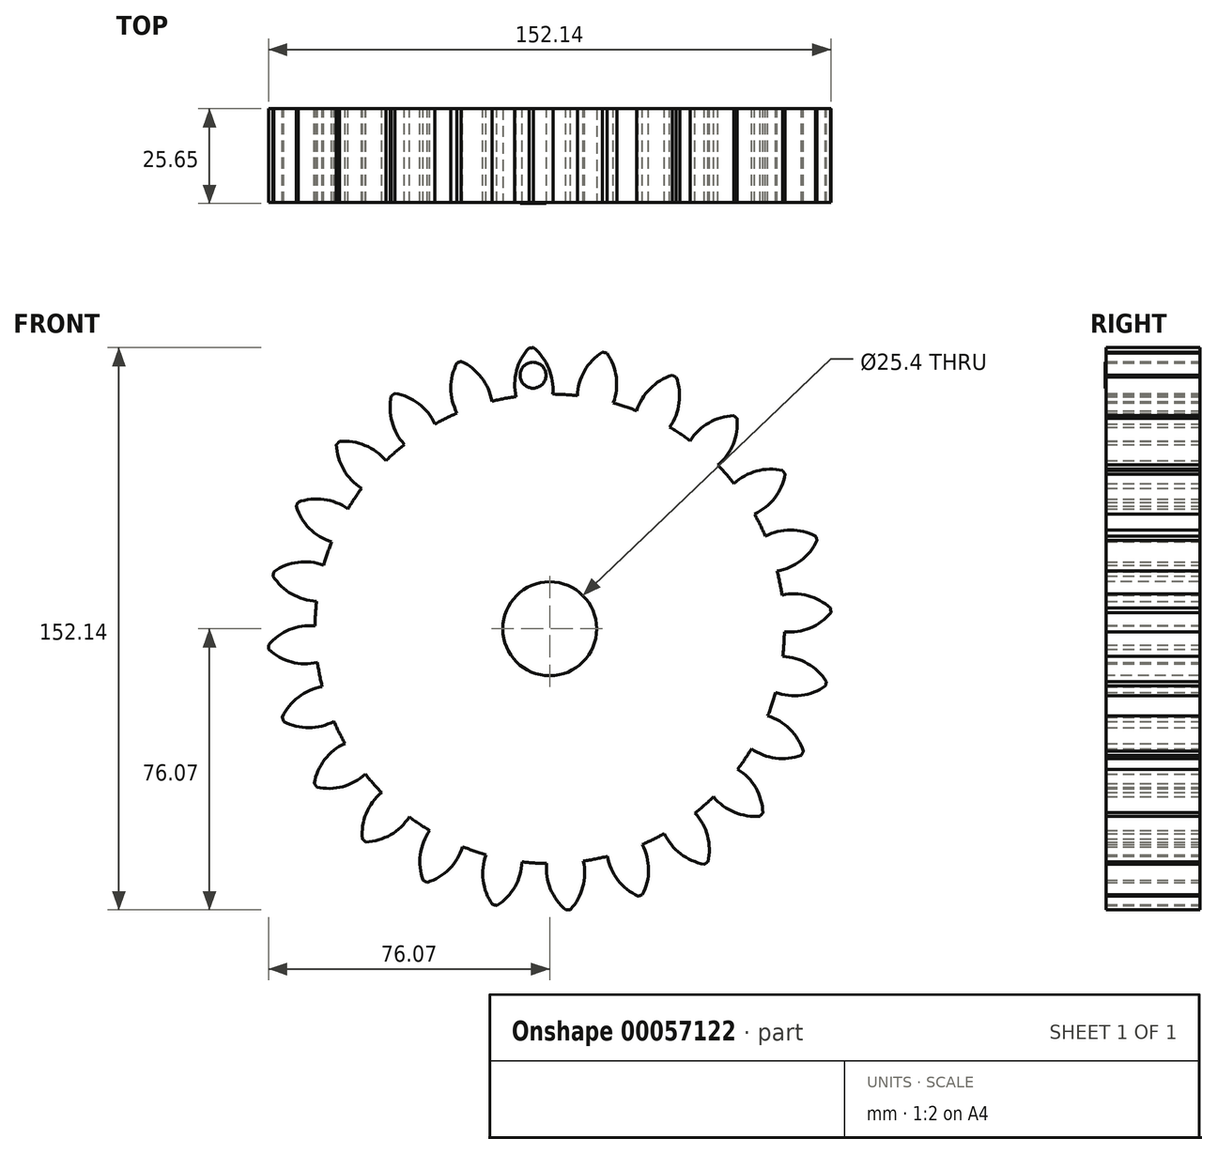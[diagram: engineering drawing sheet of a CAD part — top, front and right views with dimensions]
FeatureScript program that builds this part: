
annotation { "Feature Type Name" : "Feature", "Feature Type Description" : "" }
export const myFeature = defineFeature(function(context is Context, id is Id, definition is map)
    precondition{}
    {
        {
            var Q0;
            Q0=qCreatedBy(makeId("Front.planeOp"),FACE);
            var sketch = newSketch(context, id + "F0", { "sketchPlane" : qUnion([Q0])});
            skPoint(sketch, "E0.rect.middle", {"position": v(0, 0) * mm});
            skLineSegment(sketch, "E1", {"start": v(0, 0) * mm, "end": v(0, 76.2) * mm});
            skLineSegment(sketch, "E2", {"start": v(0, 0) * mm, "end": v(0, -76.2) * mm});
            skLineSegment(sketch, "E3", {"start": v(0, 0) * mm, "end": v(19.72, 73.6) * mm});
            skLineSegment(sketch, "E4", {"start": v(0, 0) * mm, "end": v(38.1, 66) * mm});
            skLineSegment(sketch, "E5", {"start": v(0, 0) * mm, "end": v(53.88, 53.88) * mm});
            skLineSegment(sketch, "E6", {"start": v(0, 0) * mm, "end": v(66, 38.1) * mm});
            skLineSegment(sketch, "E7", {"start": v(0, 0) * mm, "end": v(73.6, 19.72) * mm});
            skLineSegment(sketch, "E8", {"start": v(0, 0) * mm, "end": v(76.2, 0) * mm});
            skLineSegment(sketch, "E9", {"start": v(0, 0) * mm, "end": v(73.6, -19.72) * mm});
            skLineSegment(sketch, "E10", {"start": v(0, 0) * mm, "end": v(66, -38.1) * mm});
            skLineSegment(sketch, "E11", {"start": v(0, 0) * mm, "end": v(53.88, -53.88) * mm});
            skLineSegment(sketch, "E12", {"start": v(0, 0) * mm, "end": v(38.1, -66) * mm});
            skLineSegment(sketch, "E13", {"start": v(0, 0) * mm, "end": v(19.72, -73.6) * mm});
            skLineSegment(sketch, "E14", {"start": v(0, 0) * mm, "end": v(-19.72, -73.6) * mm});
            skLineSegment(sketch, "E15", {"start": v(0, 0) * mm, "end": v(-38.1, -66) * mm});
            skLineSegment(sketch, "E16", {"start": v(0, 0) * mm, "end": v(-53.88, -53.88) * mm});
            skLineSegment(sketch, "E17", {"start": v(0, 0) * mm, "end": v(-66, -38.1) * mm});
            skLineSegment(sketch, "E18", {"start": v(0, 0) * mm, "end": v(-73.6, -19.72) * mm});
            skLineSegment(sketch, "E19", {"start": v(0, 0) * mm, "end": v(-76.2, 0.07) * mm});
            skLineSegment(sketch, "E20", {"start": v(0, 0) * mm, "end": v(-73.6, 19.72) * mm});
            skLineSegment(sketch, "E21", {"start": v(0, 0) * mm, "end": v(-66, 38.1) * mm});
            skLineSegment(sketch, "E22", {"start": v(0, 0) * mm, "end": v(-53.88, 53.88) * mm});
            skLineSegment(sketch, "E23", {"start": v(0, 0) * mm, "end": v(-38.1, 66) * mm});
            skLineSegment(sketch, "E24", {"start": v(0, 0) * mm, "end": v(-19.72, 73.6) * mm});
            skCircle(sketch, "E25", {"center": v(0, 0) * mm, "radius": 76.2 * mm});
            skCircle(sketch, "E26", {"center": v(0, 0) * mm, "radius": 69.85 * mm});
            skCircle(sketch, "E27", {"center": v(0, 0) * mm, "radius": 63.5 * mm});
            skLineSegment(sketch, "E28", {"start": v(0, 0) * mm, "end": v(-4.98, 76.04) * mm});
            skLineSegment(sketch, "E29", {"start": v(0, 69.85) * mm, "end": v(-76.58, 69.85) * mm});
            skLineSegment(sketch, "E30", {"start": v(0, 69.85) * mm, "end": v(-76.5, 42) * mm});
            skLineSegment(sketch, "E31", {"start": v(-4.98, 76.04) * mm, "end": v(-7.15, 109.16) * mm});
            skLineSegment(sketch, "E32", {"start": v(0, 76.2) * mm, "end": v(0, 110.22) * mm});
            skCircle(sketch, "E33", {"center": v(0, 69.85) * mm, "radius": 14.6 * mm});
            skPoint(sketch, "E34", {"position": v(-13.72, 64.85) * mm});
            skArc(sketch, "E35", {"start": v(0.82, 63.5) * mm, "mid": v(-0.22, 70.43) * mm, "end": v(-4.37, 76.07) * mm});
            skArc(sketch, "E36.MirrorCS", {"start": v(-9.1, 62.84) * mm, "mid": v(-8.97, 69.85) * mm, "end": v(-5.6, 76) * mm});
            skSolve(sketch);
        }
        {
            var Q0;
            {var subQ1=sQuery(id+"F0.wireOp",EDGE,"E23");var subQ3=sQuery(id+"F0.wireOp",EDGE,"E27");var subQ4=makeQuery(id+"F0.imprint","INTERSECT",VERTEX,{"derivedFrom":[subQ1,subQ3]});Q0=makeQuery(id+"F0.imprint","IMPRINT",FACE,{"disambiguationData":[TD([[makeQuery(id+"F0.imprint","IMPRINT",EDGE,{"disambiguationData":[TD([[subQ4,1.0]])],"derivedFrom":subQ3}),1.0]])]});}
            var Q1;
            {var subQ1=sQuery(id+"F0.wireOp",EDGE,"E22");var subQ3=sQuery(id+"F0.wireOp",EDGE,"E27");var subQ4=makeQuery(id+"F0.imprint","INTERSECT",VERTEX,{"derivedFrom":[subQ1,subQ3]});Q1=makeQuery(id+"F0.imprint","IMPRINT",FACE,{"disambiguationData":[TD([[makeQuery(id+"F0.imprint","IMPRINT",EDGE,{"disambiguationData":[TD([[subQ4,1.0]])],"derivedFrom":subQ3}),1.0]])]});}
            var Q2;
            {var subQ1=sQuery(id+"F0.wireOp",EDGE,"E1");var subQ3=sQuery(id+"F0.wireOp",EDGE,"E33");var subQ4=makeQuery(id+"F0.imprint","INTERSECT",VERTEX,{"derivedFrom":[subQ1,subQ3]});Q2=makeQuery(id+"F0.imprint","IMPRINT",FACE,{"disambiguationData":[TD([[makeQuery(id+"F0.imprint","IMPRINT",EDGE,{"disambiguationData":[TD([[subQ4,1.0]])],"derivedFrom":subQ3}),-1.0]])]});}
            var Q3;
            {var subQ1=sQuery(id+"F0.wireOp",EDGE,"E19");var subQ3=sQuery(id+"F0.wireOp",EDGE,"E27");var subQ4=makeQuery(id+"F0.imprint","INTERSECT",VERTEX,{"derivedFrom":[subQ1,subQ3]});Q3=makeQuery(id+"F0.imprint","IMPRINT",FACE,{"disambiguationData":[TD([[makeQuery(id+"F0.imprint","IMPRINT",EDGE,{"disambiguationData":[TD([[subQ4,1.0]])],"derivedFrom":subQ3}),1.0]])]});}
            var Q4;
            {var subQ1=sQuery(id+"F0.wireOp",EDGE,"E24");var subQ3=sQuery(id+"F0.wireOp",EDGE,"E27");var subQ4=makeQuery(id+"F0.imprint","INTERSECT",VERTEX,{"derivedFrom":[subQ1,subQ3]});Q4=makeQuery(id+"F0.imprint","IMPRINT",FACE,{"disambiguationData":[TD([[makeQuery(id+"F0.imprint","IMPRINT",EDGE,{"disambiguationData":[TD([[subQ4,1.0]])],"derivedFrom":subQ3}),1.0]])]});}
            var Q5;
            {var subQ1=sQuery(id+"F0.wireOp",EDGE,"E20");var subQ3=sQuery(id+"F0.wireOp",EDGE,"E27");var subQ4=makeQuery(id+"F0.imprint","INTERSECT",VERTEX,{"derivedFrom":[subQ1,subQ3]});Q5=makeQuery(id+"F0.imprint","IMPRINT",FACE,{"disambiguationData":[TD([[makeQuery(id+"F0.imprint","IMPRINT",EDGE,{"disambiguationData":[TD([[subQ4,1.0]])],"derivedFrom":subQ3}),1.0]])]});}
            var Q6;
            {var subQ1=sQuery(id+"F0.wireOp",EDGE,"E21");var subQ3=sQuery(id+"F0.wireOp",EDGE,"E27");var subQ4=makeQuery(id+"F0.imprint","INTERSECT",VERTEX,{"derivedFrom":[subQ1,subQ3]});Q6=makeQuery(id+"F0.imprint","IMPRINT",FACE,{"disambiguationData":[TD([[makeQuery(id+"F0.imprint","IMPRINT",EDGE,{"disambiguationData":[TD([[subQ4,1.0]])],"derivedFrom":subQ3}),1.0]])]});}
            var Q7;
            {var subQ1=sQuery(id+"F0.wireOp",EDGE,"E6");var subQ3=sQuery(id+"F0.wireOp",EDGE,"E27");var subQ4=makeQuery(id+"F0.imprint","INTERSECT",VERTEX,{"derivedFrom":[subQ1,subQ3]});Q7=makeQuery(id+"F0.imprint","IMPRINT",FACE,{"disambiguationData":[TD([[makeQuery(id+"F0.imprint","IMPRINT",EDGE,{"disambiguationData":[TD([[subQ4,1.0]])],"derivedFrom":subQ3}),1.0]])]});}
            var Q8;
            {var subQ1=sQuery(id+"F0.wireOp",EDGE,"E4");var subQ3=sQuery(id+"F0.wireOp",EDGE,"E27");var subQ4=makeQuery(id+"F0.imprint","INTERSECT",VERTEX,{"derivedFrom":[subQ1,subQ3]});Q8=makeQuery(id+"F0.imprint","IMPRINT",FACE,{"disambiguationData":[TD([[makeQuery(id+"F0.imprint","IMPRINT",EDGE,{"disambiguationData":[TD([[subQ4,1.0]])],"derivedFrom":subQ3}),1.0]])]});}
            var Q9;
            {var subQ1=sQuery(id+"F0.wireOp",EDGE,"E7");var subQ3=sQuery(id+"F0.wireOp",EDGE,"E27");var subQ4=makeQuery(id+"F0.imprint","INTERSECT",VERTEX,{"derivedFrom":[subQ1,subQ3]});Q9=makeQuery(id+"F0.imprint","IMPRINT",FACE,{"disambiguationData":[TD([[makeQuery(id+"F0.imprint","IMPRINT",EDGE,{"disambiguationData":[TD([[subQ4,1.0]])],"derivedFrom":subQ3}),1.0]])]});}
            var Q10;
            {var subQ0=sQuery(id+"F0.wireOp",EDGE,"E3");var subQ5=sQuery(id+"F0.wireOp",EDGE,"E27");var subQ6=makeQuery(id+"F0.imprint","INTERSECT",VERTEX,{"derivedFrom":[subQ0,subQ5]});Q10=makeQuery(id+"F0.imprint","IMPRINT",FACE,{"disambiguationData":[TD([[makeQuery(id+"F0.imprint","IMPRINT",EDGE,{"disambiguationData":[TD([[subQ6,-1.0]])],"derivedFrom":subQ5}),1.0]])]});}
            var Q11;
            {var subQ1=sQuery(id+"F0.wireOp",EDGE,"E3");var subQ3=sQuery(id+"F0.wireOp",EDGE,"E27");var subQ4=makeQuery(id+"F0.imprint","INTERSECT",VERTEX,{"derivedFrom":[subQ1,subQ3]});Q11=makeQuery(id+"F0.imprint","IMPRINT",FACE,{"disambiguationData":[TD([[makeQuery(id+"F0.imprint","IMPRINT",EDGE,{"disambiguationData":[TD([[subQ4,1.0]])],"derivedFrom":subQ3}),1.0]])]});}
            var Q12;
            {var subQ1=sQuery(id+"F0.wireOp",EDGE,"E5");var subQ3=sQuery(id+"F0.wireOp",EDGE,"E27");var subQ4=makeQuery(id+"F0.imprint","INTERSECT",VERTEX,{"derivedFrom":[subQ1,subQ3]});Q12=makeQuery(id+"F0.imprint","IMPRINT",FACE,{"disambiguationData":[TD([[makeQuery(id+"F0.imprint","IMPRINT",EDGE,{"disambiguationData":[TD([[subQ4,1.0]])],"derivedFrom":subQ3}),1.0]])]});}
            var Q13;
            {var subQ1=sQuery(id+"F0.wireOp",EDGE,"E17");var subQ3=sQuery(id+"F0.wireOp",EDGE,"E27");var subQ4=makeQuery(id+"F0.imprint","INTERSECT",VERTEX,{"derivedFrom":[subQ1,subQ3]});Q13=makeQuery(id+"F0.imprint","IMPRINT",FACE,{"disambiguationData":[TD([[makeQuery(id+"F0.imprint","IMPRINT",EDGE,{"disambiguationData":[TD([[subQ4,1.0]])],"derivedFrom":subQ3}),1.0]])]});}
            var Q14;
            {var subQ1=sQuery(id+"F0.wireOp",EDGE,"E15");var subQ3=sQuery(id+"F0.wireOp",EDGE,"E27");var subQ4=makeQuery(id+"F0.imprint","INTERSECT",VERTEX,{"derivedFrom":[subQ1,subQ3]});Q14=makeQuery(id+"F0.imprint","IMPRINT",FACE,{"disambiguationData":[TD([[makeQuery(id+"F0.imprint","IMPRINT",EDGE,{"disambiguationData":[TD([[subQ4,1.0]])],"derivedFrom":subQ3}),1.0]])]});}
            var Q15;
            {var subQ1=sQuery(id+"F0.wireOp",EDGE,"E16");var subQ3=sQuery(id+"F0.wireOp",EDGE,"E27");var subQ4=makeQuery(id+"F0.imprint","INTERSECT",VERTEX,{"derivedFrom":[subQ1,subQ3]});Q15=makeQuery(id+"F0.imprint","IMPRINT",FACE,{"disambiguationData":[TD([[makeQuery(id+"F0.imprint","IMPRINT",EDGE,{"disambiguationData":[TD([[subQ4,1.0]])],"derivedFrom":subQ3}),1.0]])]});}
            var Q16;
            {var subQ1=sQuery(id+"F0.wireOp",EDGE,"E2");var subQ3=sQuery(id+"F0.wireOp",EDGE,"E27");var subQ4=makeQuery(id+"F0.imprint","INTERSECT",VERTEX,{"derivedFrom":[subQ1,subQ3]});Q16=makeQuery(id+"F0.imprint","IMPRINT",FACE,{"disambiguationData":[TD([[makeQuery(id+"F0.imprint","IMPRINT",EDGE,{"disambiguationData":[TD([[subQ4,1.0]])],"derivedFrom":subQ3}),1.0]])]});}
            var Q17;
            {var subQ1=sQuery(id+"F0.wireOp",EDGE,"E14");var subQ3=sQuery(id+"F0.wireOp",EDGE,"E27");var subQ4=makeQuery(id+"F0.imprint","INTERSECT",VERTEX,{"derivedFrom":[subQ1,subQ3]});Q17=makeQuery(id+"F0.imprint","IMPRINT",FACE,{"disambiguationData":[TD([[makeQuery(id+"F0.imprint","IMPRINT",EDGE,{"disambiguationData":[TD([[subQ4,1.0]])],"derivedFrom":subQ3}),1.0]])]});}
            var Q18;
            {var subQ1=sQuery(id+"F0.wireOp",EDGE,"E18");var subQ3=sQuery(id+"F0.wireOp",EDGE,"E27");var subQ4=makeQuery(id+"F0.imprint","INTERSECT",VERTEX,{"derivedFrom":[subQ1,subQ3]});Q18=makeQuery(id+"F0.imprint","IMPRINT",FACE,{"disambiguationData":[TD([[makeQuery(id+"F0.imprint","IMPRINT",EDGE,{"disambiguationData":[TD([[subQ4,1.0]])],"derivedFrom":subQ3}),1.0]])]});}
            var Q19;
            {var subQ0=sQuery(id+"F0.wireOp",EDGE,"E33");var subQ1=sQuery(id+"F0.wireOp",EDGE,"E1");var subQ2=makeQuery(id+"F0.imprint","INTERSECT",VERTEX,{"derivedFrom":[subQ1,subQ0]});Q19=makeQuery(id+"F0.imprint","IMPRINT",FACE,{"disambiguationData":[TD([[makeQuery(id+"F0.imprint","IMPRINT",EDGE,{"disambiguationData":[TD([[subQ2,-1.0]])],"derivedFrom":subQ1}),1.0]])]});}
            var Q20;
            {var subQ0=sQuery(id+"F0.wireOp",EDGE,"E27");var subQ1=makeQuery(id+"F0.imprint","INTERSECT",VERTEX,{"derivedFrom":[subQ0,sQuery(id+"F0.wireOp",EDGE,"E36.MirrorCS")]});Q20=makeQuery(id+"F0.imprint","IMPRINT",FACE,{"disambiguationData":[TD([[makeQuery(id+"F0.imprint","IMPRINT",EDGE,{"disambiguationData":[TD([[subQ1,1.0]])],"derivedFrom":subQ0}),1.0]])]});}
            var Q21;
            {var subQ0=sQuery(id+"F0.wireOp",EDGE,"E33");var subQ1=sQuery(id+"F0.wireOp",EDGE,"E1");var subQ2=makeQuery(id+"F0.imprint","INTERSECT",VERTEX,{"derivedFrom":[subQ1,subQ0]});Q21=makeQuery(id+"F0.imprint","IMPRINT",FACE,{"disambiguationData":[TD([[makeQuery(id+"F0.imprint","IMPRINT",EDGE,{"disambiguationData":[TD([[subQ2,-1.0]])],"derivedFrom":subQ1}),-1.0]])]});}
            var Q22;
            {var subQ1=sQuery(id+"F0.wireOp",EDGE,"E1");var subQ3=sQuery(id+"F0.wireOp",EDGE,"E27");var subQ4=makeQuery(id+"F0.imprint","INTERSECT",VERTEX,{"derivedFrom":[subQ1,subQ3]});Q22=makeQuery(id+"F0.imprint","IMPRINT",FACE,{"disambiguationData":[TD([[makeQuery(id+"F0.imprint","IMPRINT",EDGE,{"disambiguationData":[TD([[subQ4,-1.0]])],"derivedFrom":subQ3}),-1.0]])]});}
            var Q23;
            {var subQ0=sQuery(id+"F0.wireOp",EDGE,"E36.MirrorCS");var subQ1=sQuery(id+"F0.wireOp",EDGE,"E27");var subQ2=makeQuery(id+"F0.imprint","INTERSECT",VERTEX,{"derivedFrom":[subQ1,subQ0]});Q23=makeQuery(id+"F0.imprint","IMPRINT",FACE,{"disambiguationData":[TD([[makeQuery(id+"F0.imprint","IMPRINT",EDGE,{"disambiguationData":[TD([[subQ2,1.0]])],"derivedFrom":subQ1}),-1.0]])]});}
            var Q24;
            {var subQ0=sQuery(id+"F0.wireOp",EDGE,"E28");var subQ1=sQuery(id+"F0.wireOp",EDGE,"E26");var subQ2=makeQuery(id+"F0.imprint","INTERSECT",VERTEX,{"derivedFrom":[subQ1,subQ0]});Q24=makeQuery(id+"F0.imprint","IMPRINT",FACE,{"disambiguationData":[TD([[makeQuery(id+"F0.imprint","IMPRINT",EDGE,{"disambiguationData":[TD([[subQ2,-1.0]])],"derivedFrom":subQ1}),1.0]])]});}
            var Q25;
            {var subQ0=sQuery(id+"F0.wireOp",EDGE,"E28");var subQ1=sQuery(id+"F0.wireOp",EDGE,"E26");var subQ2=makeQuery(id+"F0.imprint","INTERSECT",VERTEX,{"derivedFrom":[subQ1,subQ0]});Q25=makeQuery(id+"F0.imprint","IMPRINT",FACE,{"disambiguationData":[TD([[makeQuery(id+"F0.imprint","IMPRINT",EDGE,{"disambiguationData":[TD([[subQ2,-1.0]])],"derivedFrom":subQ1}),-1.0]])]});}
            var Q26;
            {var subQ0=sQuery(id+"F0.wireOp",EDGE,"E28");var subQ5=sQuery(id+"F0.wireOp",EDGE,"E29");var subQ6=makeQuery(id+"F0.imprint","INTERSECT",VERTEX,{"derivedFrom":[subQ0,subQ5]});Q26=makeQuery(id+"F0.imprint","IMPRINT",FACE,{"disambiguationData":[TD([[makeQuery(id+"F0.imprint","IMPRINT",EDGE,{"disambiguationData":[TD([[subQ6,-1.0]])],"derivedFrom":subQ5}),-1.0]])]});}
            var Q27;
            {var subQ1=sQuery(id+"F0.wireOp",EDGE,"E25");var subQ3=sQuery(id+"F0.wireOp",EDGE,"E35");var subQ4=makeQuery(id+"F0.imprint","INTERSECT",VERTEX,{"derivedFrom":[subQ1,subQ3]});Q27=makeQuery(id+"F0.imprint","IMPRINT",FACE,{"disambiguationData":[TD([[makeQuery(id+"F0.imprint","IMPRINT",EDGE,{"disambiguationData":[TD([[subQ4,-1.0]])],"derivedFrom":subQ1}),1.0]])]});}
            var Q28;
            {var subQ0=sQuery(id+"F0.wireOp",EDGE,"E35");var subQ3=sQuery(id+"F0.wireOp",EDGE,"E27");var subQ5=makeQuery(id+"F0.imprint","INTERSECT",VERTEX,{"derivedFrom":[subQ3,subQ0]});Q28=makeQuery(id+"F0.imprint","IMPRINT",FACE,{"disambiguationData":[TD([[makeQuery(id+"F0.imprint","IMPRINT",EDGE,{"disambiguationData":[TD([[subQ5,-1.0]])],"derivedFrom":subQ3}),-1.0]])]});}
            var Q29;
            {var subQ1=sQuery(id+"F0.wireOp",EDGE,"E26");var subQ3=sQuery(id+"F0.wireOp",EDGE,"E28");var subQ4=makeQuery(id+"F0.imprint","INTERSECT",VERTEX,{"derivedFrom":[subQ1,subQ3]});Q29=makeQuery(id+"F0.imprint","IMPRINT",FACE,{"disambiguationData":[TD([[makeQuery(id+"F0.imprint","IMPRINT",EDGE,{"disambiguationData":[TD([[subQ4,-1.0]])],"derivedFrom":subQ3}),-1.0]])]});}
            var Q30;
            {var subQ1=sQuery(id+"F0.wireOp",EDGE,"E26");var subQ3=sQuery(id+"F0.wireOp",EDGE,"E28");var subQ4=makeQuery(id+"F0.imprint","INTERSECT",VERTEX,{"derivedFrom":[subQ1,subQ3]});Q30=makeQuery(id+"F0.imprint","IMPRINT",FACE,{"disambiguationData":[TD([[makeQuery(id+"F0.imprint","IMPRINT",EDGE,{"disambiguationData":[TD([[subQ4,1.0]])],"derivedFrom":subQ3}),-1.0]])]});}
            var Q31;
            {var subQ1=sQuery(id+"F0.wireOp",EDGE,"E10");var subQ3=sQuery(id+"F0.wireOp",EDGE,"E27");var subQ4=makeQuery(id+"F0.imprint","INTERSECT",VERTEX,{"derivedFrom":[subQ1,subQ3]});Q31=makeQuery(id+"F0.imprint","IMPRINT",FACE,{"disambiguationData":[TD([[makeQuery(id+"F0.imprint","IMPRINT",EDGE,{"disambiguationData":[TD([[subQ4,1.0]])],"derivedFrom":subQ3}),1.0]])]});}
            var Q32;
            {var subQ1=sQuery(id+"F0.wireOp",EDGE,"E9");var subQ3=sQuery(id+"F0.wireOp",EDGE,"E27");var subQ4=makeQuery(id+"F0.imprint","INTERSECT",VERTEX,{"derivedFrom":[subQ1,subQ3]});Q32=makeQuery(id+"F0.imprint","IMPRINT",FACE,{"disambiguationData":[TD([[makeQuery(id+"F0.imprint","IMPRINT",EDGE,{"disambiguationData":[TD([[subQ4,1.0]])],"derivedFrom":subQ3}),1.0]])]});}
            var Q33;
            {var subQ1=sQuery(id+"F0.wireOp",EDGE,"E8");var subQ3=sQuery(id+"F0.wireOp",EDGE,"E27");var subQ4=makeQuery(id+"F0.imprint","INTERSECT",VERTEX,{"derivedFrom":[subQ1,subQ3]});Q33=makeQuery(id+"F0.imprint","IMPRINT",FACE,{"disambiguationData":[TD([[makeQuery(id+"F0.imprint","IMPRINT",EDGE,{"disambiguationData":[TD([[subQ4,1.0]])],"derivedFrom":subQ3}),1.0]])]});}
            var Q34;
            {var subQ1=sQuery(id+"F0.wireOp",EDGE,"E11");var subQ3=sQuery(id+"F0.wireOp",EDGE,"E27");var subQ4=makeQuery(id+"F0.imprint","INTERSECT",VERTEX,{"derivedFrom":[subQ1,subQ3]});Q34=makeQuery(id+"F0.imprint","IMPRINT",FACE,{"disambiguationData":[TD([[makeQuery(id+"F0.imprint","IMPRINT",EDGE,{"disambiguationData":[TD([[subQ4,1.0]])],"derivedFrom":subQ3}),1.0]])]});}
            var Q35;
            {var subQ1=sQuery(id+"F0.wireOp",EDGE,"E2");var subQ3=sQuery(id+"F0.wireOp",EDGE,"E27");var subQ4=makeQuery(id+"F0.imprint","INTERSECT",VERTEX,{"derivedFrom":[subQ1,subQ3]});Q35=makeQuery(id+"F0.imprint","IMPRINT",FACE,{"disambiguationData":[TD([[makeQuery(id+"F0.imprint","IMPRINT",EDGE,{"disambiguationData":[TD([[subQ4,-1.0]])],"derivedFrom":subQ3}),1.0]])]});}
            var Q36;
            {var subQ1=sQuery(id+"F0.wireOp",EDGE,"E12");var subQ3=sQuery(id+"F0.wireOp",EDGE,"E27");var subQ4=makeQuery(id+"F0.imprint","INTERSECT",VERTEX,{"derivedFrom":[subQ1,subQ3]});Q36=makeQuery(id+"F0.imprint","IMPRINT",FACE,{"disambiguationData":[TD([[makeQuery(id+"F0.imprint","IMPRINT",EDGE,{"disambiguationData":[TD([[subQ4,1.0]])],"derivedFrom":subQ3}),1.0]])]});}
            extrude(context, id + "F1", {"entities" : qUnion([Q0, Q1, Q2, Q3, Q4, Q5, Q6, Q7, Q8, Q9, Q10, Q11, Q12, Q13, Q14, Q15, Q16, Q17, Q18, Q19, Q20, Q21, Q22, Q23, Q24, Q25, Q26, Q27, Q28, Q29, Q30, Q31, Q32, Q33, Q34, Q35, Q36]), "depth" : 25.4 * mm, "symmetric" : true});
        }
        {
            var Q0;
            Q0=makeQuery(id+"F1.opExtrude","SWEPT_BODY",BODY,{"disambiguationData":[OSD([sQuery(id+"F0.wireOp",EDGE,"E25"),sQuery(id+"F0.wireOp",EDGE,"E27"),sQuery(id+"F0.wireOp",EDGE,"E35"),sQuery(id+"F0.wireOp",EDGE,"E36.MirrorCS")])]});
            var Q1;
            Q1=makeQuery(id+"F1.opExtrude","SWEPT_FACE",FACE,{"disambiguationData":[OSD([sQuery(id+"F0.wireOp",EDGE,"E27")])]});
            circularPattern(context, id + "F2", {"operationType" : NewBodyOperationType.ADD, "entities" : qUnion([Q0]), "axis" : qUnion([Q1]), "angle" : 15 * degree, "instanceCount" : 24});
        }
        {
            var Q0;
            Q0=makeQuery(id+"F1.opExtrude","CAP_FACE",FACE,{"disambiguationData":[OSD([sQuery(id+"F0.wireOp",EDGE,"E25"),sQuery(id+"F0.wireOp",EDGE,"E27"),sQuery(id+"F0.wireOp",EDGE,"E35"),sQuery(id+"F0.wireOp",EDGE,"E36.MirrorCS")])],"isStart":false});
            var sketch = newSketch(context, id + "F3", { "sketchPlane" : qUnion([Q0])});
            skPoint(sketch, "E37", {"position": v(0, 0) * mm});
            skSolve(sketch);
        }
        {
            var Q0;
            Q0=sQuery(id+"F3.wireOp",VERTEX,"E37");
            var Q1;
            Q1=makeQuery(id+"F1.opExtrude","SWEPT_BODY",BODY,{"disambiguationData":[OSD([sQuery(id+"F0.wireOp",EDGE,"E25"),sQuery(id+"F0.wireOp",EDGE,"E27"),sQuery(id+"F0.wireOp",EDGE,"E35"),sQuery(id+"F0.wireOp",EDGE,"E36.MirrorCS")])]});
            hole(context, id + "F4", {"style" : HoleStyle.SIMPLE, "holeDiameter" : 25.4 * mm, "endStyle" : HoleEndStyle.THROUGH, "locations" : qUnion([Q0]), "scope" : qUnion([Q1])});
        }
        {
            var Q0;
            {var subQ0=makeQuery(id+"F1.opExtrude","CAP_FACE",FACE,{"disambiguationData":[OSD([sQuery(id+"F0.wireOp",EDGE,"E25"),sQuery(id+"F0.wireOp",EDGE,"E27"),sQuery(id+"F0.wireOp",EDGE,"E35"),sQuery(id+"F0.wireOp",EDGE,"E36.MirrorCS")])],"isStart":false});Q0=makeQuery(id+"F2.boolean.opBoolean","MERGE",FACE,{"derivedFrom":[subQ0,makeQuery(id+"F2.opPattern","COPY",FACE,{"derivedFrom":subQ0,"instanceName":"1"}),makeQuery(id+"F2.opPattern","COPY",FACE,{"derivedFrom":subQ0,"instanceName":"2"}),makeQuery(id+"F2.opPattern","COPY",FACE,{"derivedFrom":subQ0,"instanceName":"3"}),makeQuery(id+"F2.opPattern","COPY",FACE,{"derivedFrom":subQ0,"instanceName":"4"}),makeQuery(id+"F2.opPattern","COPY",FACE,{"derivedFrom":subQ0,"instanceName":"5"}),makeQuery(id+"F2.opPattern","COPY",FACE,{"derivedFrom":subQ0,"instanceName":"6"}),makeQuery(id+"F2.opPattern","COPY",FACE,{"derivedFrom":subQ0,"instanceName":"7"}),makeQuery(id+"F2.opPattern","COPY",FACE,{"derivedFrom":subQ0,"instanceName":"8"}),makeQuery(id+"F2.opPattern","COPY",FACE,{"derivedFrom":subQ0,"instanceName":"9"}),makeQuery(id+"F2.opPattern","COPY",FACE,{"derivedFrom":subQ0,"instanceName":"10"}),makeQuery(id+"F2.opPattern","COPY",FACE,{"derivedFrom":subQ0,"instanceName":"11"}),makeQuery(id+"F2.opPattern","COPY",FACE,{"derivedFrom":subQ0,"instanceName":"12"}),makeQuery(id+"F2.opPattern","COPY",FACE,{"derivedFrom":subQ0,"instanceName":"13"}),makeQuery(id+"F2.opPattern","COPY",FACE,{"derivedFrom":subQ0,"instanceName":"14"}),makeQuery(id+"F2.opPattern","COPY",FACE,{"derivedFrom":subQ0,"instanceName":"15"}),makeQuery(id+"F2.opPattern","COPY",FACE,{"derivedFrom":subQ0,"instanceName":"16"}),makeQuery(id+"F2.opPattern","COPY",FACE,{"derivedFrom":subQ0,"instanceName":"17"}),makeQuery(id+"F2.opPattern","COPY",FACE,{"derivedFrom":subQ0,"instanceName":"18"}),makeQuery(id+"F2.opPattern","COPY",FACE,{"derivedFrom":subQ0,"instanceName":"19"}),makeQuery(id+"F2.opPattern","COPY",FACE,{"derivedFrom":subQ0,"instanceName":"20"}),makeQuery(id+"F2.opPattern","COPY",FACE,{"derivedFrom":subQ0,"instanceName":"21"}),makeQuery(id+"F2.opPattern","COPY",FACE,{"derivedFrom":subQ0,"instanceName":"22"}),makeQuery(id+"F2.opPattern","COPY",FACE,{"derivedFrom":subQ0,"instanceName":"23"})]});}
            var sketch = newSketch(context, id + "F5", { "sketchPlane" : qUnion([Q0])});
            skCircle(sketch, "E38", {"center": v(-4.51, 68.62) * mm, "radius": 3.51 * mm});
            skSolve(sketch);
        }
        {
            var Q0;
            Q0=makeQuery(id+"F5.imprint","IMPRINT",FACE,{"disambiguationData":[TD([[makeQuery(id+"F5.imprint","IMPRINT",EDGE,{"derivedFrom":sQuery(id+"F5.wireOp",EDGE,"E38")}),1.0]])]});
            extrude(context, id + "F6", {"entities" : qUnion([Q0]), "operationType" : NewBodyOperationType.ADD, "depth" : 0.25 * mm});
        }
    });
